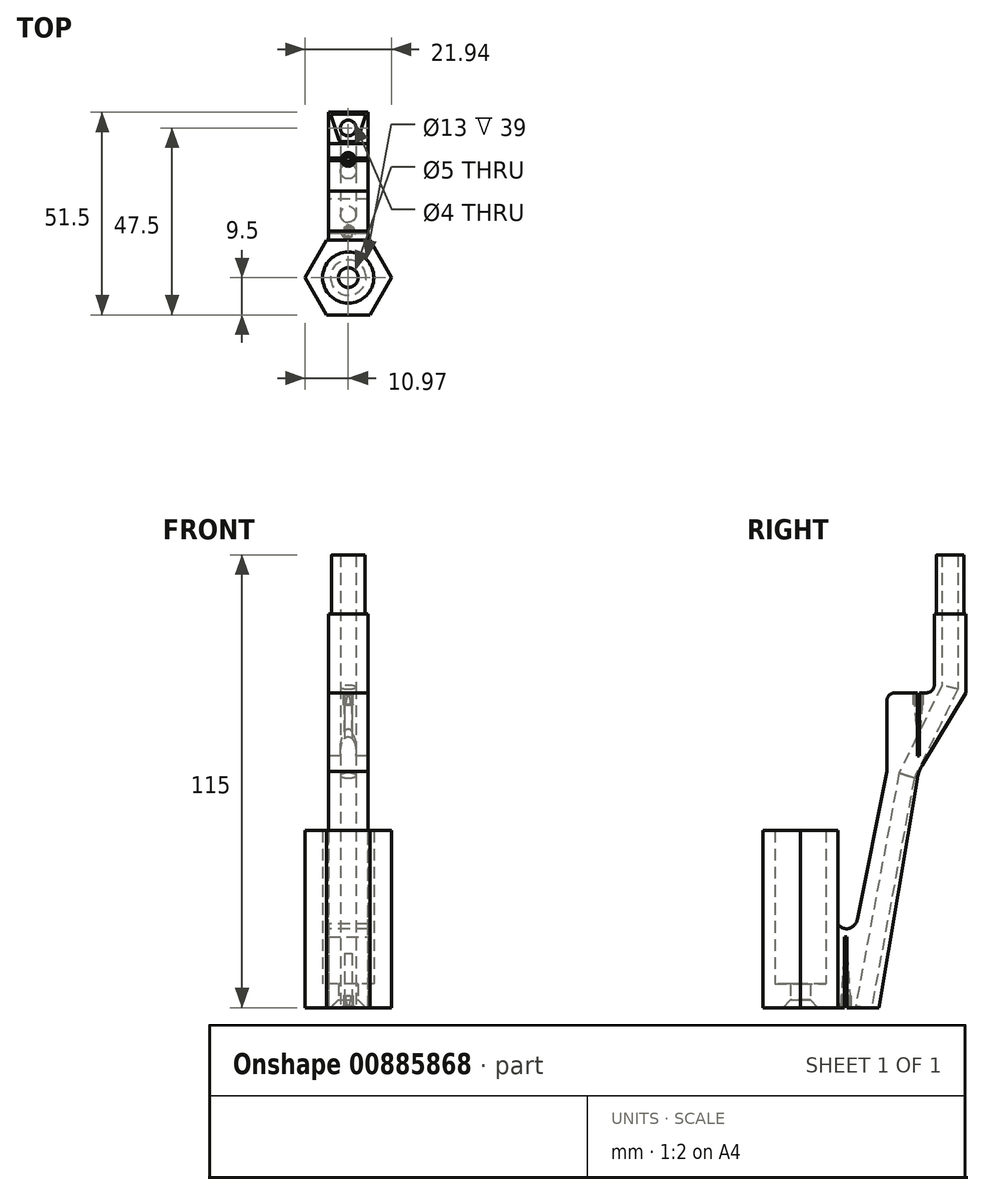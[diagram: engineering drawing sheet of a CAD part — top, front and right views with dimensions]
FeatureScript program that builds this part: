
annotation { "Feature Type Name" : "Feature", "Feature Type Description" : "" }
export const myFeature = defineFeature(function(context is Context, id is Id, definition is map)
    precondition{}
    {
        {
            var Q0;
            Q0=qCreatedBy(makeId("Top.planeOp"),FACE);
            var sketch = newSketch(context, id + "F0", { "sketchPlane" : qUnion([Q0])});
            skCircle(sketch, "E0", {"center": v(0, 0) * mm, "radius": 6.5 * mm});
            skCircle(sketch, "E1.cCircle", {"center": v(0, 0) * mm, "radius": 9.5 * mm, "construction": true});
            skLineSegment(sketch, "E1.0", {"start": v(10.97, 0) * mm, "end": v(5.48, -9.5) * mm});
            skLineSegment(sketch, "E1.1", {"start": v(5.48, -9.5) * mm, "end": v(-5.48, -9.5) * mm});
            skLineSegment(sketch, "E1.2", {"start": v(-5.48, -9.5) * mm, "end": v(-10.97, 0) * mm});
            skLineSegment(sketch, "E1.3", {"start": v(-10.97, 0) * mm, "end": v(-5.48, 9.5) * mm});
            skLineSegment(sketch, "E1.4", {"start": v(-5.48, 9.5) * mm, "end": v(5.48, 9.5) * mm});
            skLineSegment(sketch, "E1.5", {"start": v(5.48, 9.5) * mm, "end": v(10.97, 0) * mm});
            skPoint(sketch, "E1.0.midPoint", {"position": v(8.23, -4.75) * mm});
            skSolve(sketch);
        }
        {
            var Q0;
            Q0=makeQuery(id+"F0.imprint","IMPRINT",FACE,{"disambiguationData":[TD([[makeQuery(id+"F0.imprint","IMPRINT",EDGE,{"derivedFrom":sQuery(id+"F0.wireOp",EDGE,"E0")}),-1.0]])]});
            extrude(context, id + "F1", {"entities" : qUnion([Q0]), "depth" : 45 * mm, "offsetDistance" : 25 * mm});
        }
        {
            var Q0;
            Q0=makeQuery(id+"F0.imprint","IMPRINT",FACE,{"disambiguationData":[TD([[makeQuery(id+"F0.imprint","IMPRINT",EDGE,{"derivedFrom":sQuery(id+"F0.wireOp",EDGE,"E0")}),1.0]])]});
            extrude(context, id + "F2", {"entities" : qUnion([Q0]), "operationType" : NewBodyOperationType.ADD, "depth" : 6 * mm, "offsetDistance" : 25 * mm});
        }
        {
            var Q0;
            Q0=sQuery(id+"F0.wireOp",VERTEX,"E0.center");
            var Q1;
            Q1=makeQuery(id+"F1.opExtrude","SWEPT_BODY",BODY,{"disambiguationData":[OSD([sQuery(id+"F0.wireOp",EDGE,"E0"),sQuery(id+"F0.wireOp",EDGE,"E1.0"),sQuery(id+"F0.wireOp",EDGE,"E1.1"),sQuery(id+"F0.wireOp",EDGE,"E1.2"),sQuery(id+"F0.wireOp",EDGE,"E1.3"),sQuery(id+"F0.wireOp",EDGE,"E1.4"),sQuery(id+"F0.wireOp",EDGE,"E1.5")])]});
            hole(context, id + "F3", {"style" : HoleStyle.C_SINK, "endStyle" : HoleEndStyle.THROUGH, "oppositeDirection" : true, "holeDiameter" : 5 * mm, "cSinkDiameter" : 9 * mm, "cSinkAngle" : 90 * degree, "majorDiameter" : 5 * mm, "isTappedThrough" : true, "tappedDepth" : 12 * mm, "tapClearance" : 3, "locations" : qUnion([Q0]), "scope" : qUnion([Q1])});
        }
        {
            var Q0;
            Q0=qCreatedBy(makeId("Right.planeOp"),FACE);
            var sketch = newSketch(context, id + "F4", { "sketchPlane" : qUnion([Q0])});
            skLineSegment(sketch, "E2", {"start": v(0, -69.7) * mm, "end": v(0, 100) * mm, "construction": true});
            skLineSegment(sketch, "E3", {"start": v(22, 78) * mm, "end": v(22, 60) * mm});
            skLineSegment(sketch, "E4", {"start": v(34, 100) * mm, "end": v(34, 82) * mm});
            skLineSegment(sketch, "E5", {"start": v(42, 100) * mm, "end": v(34, 100) * mm});
            skLineSegment(sketch, "E6", {"start": v(22, 60) * mm, "end": v(14.48, 22.41) * mm});
            skLineSegment(sketch, "E7", {"start": v(12, 20) * mm, "end": v(11.54, 20) * mm});
            skLineSegment(sketch, "E8", {"start": v(20, 0) * mm, "end": v(29.69, 58.13) * mm});
            skLineSegment(sketch, "E9", {"start": v(32, 80) * mm, "end": v(24, 80) * mm});
            skLineSegment(sketch, "E10", {"start": v(20, 0) * mm, "end": v(8.5, 0) * mm});
            skLineSegment(sketch, "E11", {"start": v(42, 80) * mm, "end": v(30.98, 61.63) * mm});
            skLineSegment(sketch, "E12", {"start": v(42, 100) * mm, "end": v(42, 100) * mm});
            skLineSegment(sketch, "E13", {"start": v(42, 100) * mm, "end": v(42, 80) * mm});
            skPoint(sketch, "E14.visualSharp", {"position": v(20, 0) * mm});
            skPoint(sketch, "E15.visualSharp", {"position": v(30, 60) * mm});
            skArc(sketch, "E15.filletArc", {"start": v(30.98, 61.63) * mm, "mid": v(30.17, 59.94) * mm, "end": v(29.69, 58.13) * mm});
            skPoint(sketch, "E16.visualSharp", {"position": v(34, 80) * mm});
            skArc(sketch, "E16.filletArc", {"start": v(32, 80) * mm, "mid": v(33.41, 80.59) * mm, "end": v(34, 82) * mm});
            skPoint(sketch, "E17.visualSharp", {"position": v(22, 80) * mm});
            skArc(sketch, "E17.filletArc", {"start": v(24, 80) * mm, "mid": v(22.59, 79.41) * mm, "end": v(22, 78) * mm});
            skPoint(sketch, "E18.visualSharp", {"position": v(34, 100) * mm});
            skPoint(sketch, "E19.visualSharp", {"position": v(14, 20) * mm});
            skArc(sketch, "E19.filletArc", {"start": v(11.54, 20) * mm, "mid": v(13.44, 20.68) * mm, "end": v(14.48, 22.41) * mm});
            skLineSegment(sketch, "E20", {"start": v(9, 23) * mm, "end": v(9, 45) * mm});
            skPoint(sketch, "E21.visualSharp", {"position": v(9, 20) * mm});
            skArc(sketch, "E21.filletArc", {"start": v(9, 23) * mm, "mid": v(9.88, 20.88) * mm, "end": v(12, 20) * mm});
            skLineSegment(sketch, "E22", {"start": v(9, 45) * mm, "end": v(8.5, 45) * mm});
            skLineSegment(sketch, "E23", {"start": v(8.5, 45) * mm, "end": v(8.5, 0) * mm});
            skLineSegment(sketch, "E24", {"start": v(16, 0) * mm, "end": v(27, 58.98) * mm});
            skLineSegment(sketch, "E25", {"start": v(27, 58.98) * mm, "end": v(38, 81.43) * mm});
            skLineSegment(sketch, "E26", {"start": v(38, 81.43) * mm, "end": v(38, 100) * mm});
            skPoint(sketch, "E27", {"position": v(38, 100) * mm});
            skLineSegment(sketch, "E28", {"start": v(38, 100) * mm, "end": v(38, 115) * mm});
            skSolve(sketch);
        }
        {
            var Q0;
            Q0 = qSketchRegion(id + "F4", true);
            extrude(context, id + "F5", {"entities" : qUnion([Q0]), "operationType" : NewBodyOperationType.ADD, "endBound" : BoundingType.SYMMETRIC, "depth" : 10 * mm, "offsetDistance" : 25 * mm});
        }
        {
            var Q0;
            Q0=makeQuery(id+"F5.opExtrude","SWEPT_FACE",FACE,{"disambiguationData":[OSD([sQuery(id+"F4.wireOp",EDGE,"E9")])]});
            var sketch = newSketch(context, id + "F6", { "sketchPlane" : qUnion([Q0])});
            skPoint(sketch, "E29", {"position": v(0, 30) * mm});
            skLineSegment(sketch, "E30.bottom", {"start": v(5, 29.7) * mm, "end": v(-5, 29.7) * mm});
            skLineSegment(sketch, "E30.top", {"start": v(5, 30.3) * mm, "end": v(-5, 30.3) * mm});
            skLineSegment(sketch, "E30.left", {"start": v(5, 29.7) * mm, "end": v(5, 30.3) * mm});
            skLineSegment(sketch, "E30.right", {"start": v(-5, 29.7) * mm, "end": v(-5, 30.3) * mm});
            skSolve(sketch);
        }
        {
            var Q0;
            Q0=sQuery(id+"F6.wireOp",VERTEX,"E29");
            var Q1;
            Q1=makeQuery(id+"F5.opExtrude","SWEPT_BODY",BODY,{"disambiguationData":[OSD([sQuery(id+"F4.wireOp",EDGE,"E3"),sQuery(id+"F4.wireOp",EDGE,"H4g1pZ8y-bMZj-Yfp0-DUyw-PG9j3wVcMHNI"),sQuery(id+"F4.wireOp",EDGE,"ujzuVlM0-uvlb-eoDg-W0Gq-mJ8zsjEyDlQp"),sQuery(id+"F4.wireOp",EDGE,"E4"),sQuery(id+"F4.wireOp",EDGE,"iK9Z7oXa-DGHX-qq8q-kj9N-MazxaWKy61rx"),sQuery(id+"F4.wireOp",EDGE,"E5"),sQuery(id+"F4.wireOp",EDGE,"E6"),sQuery(id+"F4.wireOp",EDGE,"E7"),sQuery(id+"F4.wireOp",EDGE,"E8"),sQuery(id+"F4.wireOp",EDGE,"E9"),sQuery(id+"F4.wireOp",EDGE,"E10"),sQuery(id+"F4.wireOp",EDGE,"c5ac7997-6308-41a4-87d6-0d990d36ccd3")])]});
            var Q2;
            Q2=makeQuery(id+"F1.opExtrude","SWEPT_BODY",BODY,{"disambiguationData":[OSD([sQuery(id+"F0.wireOp",EDGE,"E0"),sQuery(id+"F0.wireOp",EDGE,"E1.0"),sQuery(id+"F0.wireOp",EDGE,"E1.1"),sQuery(id+"F0.wireOp",EDGE,"E1.2"),sQuery(id+"F0.wireOp",EDGE,"E1.3"),sQuery(id+"F0.wireOp",EDGE,"E1.4"),sQuery(id+"F0.wireOp",EDGE,"E1.5")])]});
            hole(context, id + "F7", {"style" : HoleStyle.C_SINK, "endStyle" : HoleEndStyle.BLIND, "holeDiameter" : 2.5 * mm, "cSinkDiameter" : 3.5 * mm, "cSinkAngle" : 90 * degree, "majorDiameter" : 5 * mm, "holeDepth" : 3 * mm, "isTappedThrough" : true, "tappedDepth" : 12 * mm, "tapClearance" : 3, "locations" : qUnion([Q0]), "scope" : qUnion([Q1, Q2])});
        }
        {
            var Q0;
            Q0=makeQuery(id+"F6.imprint","IMPRINT",FACE,{"disambiguationData":[TD([[makeQuery(id+"F6.imprint","IMPRINT",EDGE,{"derivedFrom":sQuery(id+"F6.wireOp",EDGE,"E30.bottom")}),-1.0]])]});
            extrude(context, id + "F8", {"entities" : qUnion([Q0]), "operationType" : NewBodyOperationType.REMOVE, "oppositeDirection" : true, "depth" : 16 * mm, "offsetDistance" : 25 * mm});
        }
        {
            var Q0;
            Q0=qCreatedBy(makeId("Right.planeOp"),FACE);
            var sketch = newSketch(context, id + "F9", { "sketchPlane" : qUnion([Q0])});
            skPoint(sketch, "E31.0", {"position": v(30, 60) * mm});
            skPoint(sketch, "E31.1", {"position": v(30, 64) * mm});
            skLineSegment(sketch, "E32", {"start": v(28.75, 79.5) * mm, "end": v(31.25, 79.5) * mm});
            skLineSegment(sketch, "E33", {"start": v(28.75, 79.5) * mm, "end": v(30, 64) * mm});
            skLineSegment(sketch, "E34", {"start": v(30, 64) * mm, "end": v(31.25, 79.5) * mm});
            skPoint(sketch, "E35.0", {"position": v(28.75, 79.5) * mm});
            skPoint(sketch, "E35.1", {"position": v(31.25, 79.5) * mm});
            skSolve(sketch);
        }
        {
            var Q0;
            Q0 = qSketchRegion(id + "F9", true);
            extrude(context, id + "F10", {"entities" : qUnion([Q0]), "operationType" : NewBodyOperationType.REMOVE, "endBound" : BoundingType.SYMMETRIC, "depth" : 2 * mm, "offsetDistance" : 25 * mm});
        }
        {
            var Q0;
            Q0=makeQuery(id+"F5.opExtrude","SWEPT_FACE",FACE,{"disambiguationData":[OSD([sQuery(id+"F4.wireOp",EDGE,"E10")])]});
            var sketch = newSketch(context, id + "F11", { "sketchPlane" : qUnion([Q0])});
            skLineSegment(sketch, "E36", {"start": v(-5, -11.24) * mm, "end": v(5, -11.24) * mm});
            skLineSegment(sketch, "E37", {"start": v(5, -11.24) * mm, "end": v(5, -11.84) * mm});
            skLineSegment(sketch, "E38", {"start": v(5, -11.84) * mm, "end": v(-5, -11.84) * mm});
            skLineSegment(sketch, "E39", {"start": v(-5, -11.84) * mm, "end": v(-5, -11.24) * mm});
            skLineSegment(sketch, "E40", {"start": v(0, -11.24) * mm, "end": v(0, -11.84) * mm, "construction": true});
            skPoint(sketch, "E41", {"position": v(0, -11.54) * mm});
            skSolve(sketch);
        }
        {
            var Q0;
            Q0=sQuery(id+"F11.wireOp",VERTEX,"E41");
            var Q1;
            Q1=makeQuery(id+"F5.opExtrude","SWEPT_BODY",BODY,{"disambiguationData":[OSD([sQuery(id+"F4.wireOp",EDGE,"E3"),sQuery(id+"F4.wireOp",EDGE,"H4g1pZ8y-bMZj-Yfp0-DUyw-PG9j3wVcMHNI"),sQuery(id+"F4.wireOp",EDGE,"ujzuVlM0-uvlb-eoDg-W0Gq-mJ8zsjEyDlQp"),sQuery(id+"F4.wireOp",EDGE,"E4"),sQuery(id+"F4.wireOp",EDGE,"iK9Z7oXa-DGHX-qq8q-kj9N-MazxaWKy61rx"),sQuery(id+"F4.wireOp",EDGE,"E5"),sQuery(id+"F4.wireOp",EDGE,"E6"),sQuery(id+"F4.wireOp",EDGE,"E7"),sQuery(id+"F4.wireOp",EDGE,"E8"),sQuery(id+"F4.wireOp",EDGE,"E9"),sQuery(id+"F4.wireOp",EDGE,"E10"),sQuery(id+"F4.wireOp",EDGE,"c5ac7997-6308-41a4-87d6-0d990d36ccd3")])]});
            var Q2;
            Q2=makeQuery(id+"F1.opExtrude","SWEPT_BODY",BODY,{"disambiguationData":[OSD([sQuery(id+"F0.wireOp",EDGE,"E0"),sQuery(id+"F0.wireOp",EDGE,"E1.0"),sQuery(id+"F0.wireOp",EDGE,"E1.1"),sQuery(id+"F0.wireOp",EDGE,"E1.2"),sQuery(id+"F0.wireOp",EDGE,"E1.3"),sQuery(id+"F0.wireOp",EDGE,"E1.4"),sQuery(id+"F0.wireOp",EDGE,"E1.5")])]});
            hole(context, id + "F12", {"style" : HoleStyle.C_SINK, "endStyle" : HoleEndStyle.BLIND, "holeDiameter" : 2.5 * mm, "cSinkDiameter" : 3.5 * mm, "cSinkAngle" : 90 * degree, "majorDiameter" : 5 * mm, "holeDepth" : 3 * mm, "isTappedThrough" : true, "tappedDepth" : 12 * mm, "tapClearance" : 3, "locations" : qUnion([Q0]), "scope" : qUnion([Q1, Q2])});
        }
        {
            var Q0;
            Q0=makeQuery(id+"F11.imprint","IMPRINT",FACE,{"disambiguationData":[TD([[makeQuery(id+"F11.imprint","IMPRINT",EDGE,{"derivedFrom":sQuery(id+"F11.wireOp",EDGE,"E36")}),-1.0]])]});
            extrude(context, id + "F13", {"entities" : qUnion([Q0]), "operationType" : NewBodyOperationType.REMOVE, "oppositeDirection" : true, "depth" : 18 * mm, "offsetDistance" : 25 * mm});
        }
        {
            var Q0;
            Q0=qCreatedBy(makeId("Right.planeOp"),FACE);
            var sketch = newSketch(context, id + "F14", { "sketchPlane" : qUnion([Q0])});
            skPoint(sketch, "E42.0", {"position": v(10.3, 0.5) * mm});
            skPoint(sketch, "E42.1", {"position": v(12.8, 0.5) * mm});
            skPoint(sketch, "E43.0", {"position": v(11.84, 18) * mm});
            skPoint(sketch, "E44.0", {"position": v(11.24, 18) * mm});
            skLineSegment(sketch, "E45", {"start": v(11.24, 18) * mm, "end": v(11.84, 18) * mm, "construction": true});
            skPoint(sketch, "E46", {"position": v(11.54, 18) * mm});
            skLineSegment(sketch, "E47", {"start": v(10.3, 0.5) * mm, "end": v(11.54, 18) * mm});
            skLineSegment(sketch, "E48", {"start": v(11.54, 18) * mm, "end": v(12.8, 0.5) * mm});
            skLineSegment(sketch, "E49", {"start": v(10.3, 0.5) * mm, "end": v(12.8, 0.5) * mm});
            skSolve(sketch);
        }
        {
            var Q0;
            Q0 = qSketchRegion(id + "F14", true);
            extrude(context, id + "F15", {"entities" : qUnion([Q0]), "operationType" : NewBodyOperationType.REMOVE, "endBound" : BoundingType.SYMMETRIC, "depth" : 2 * mm, "offsetDistance" : 25 * mm});
        }
        {
            var Q0;
            Q0=makeQuery(id+"F5.opExtrude","SWEPT_FACE",FACE,{"disambiguationData":[OSD([sQuery(id+"F4.wireOp",EDGE,"E5")])]});
            var sketch = newSketch(context, id + "F16", { "sketchPlane" : qUnion([Q0])});
            skLineSegment(sketch, "E50", {"start": v(-3.68, 41.5) * mm, "end": v(3.68, 41.5) * mm});
            skLineSegment(sketch, "E51", {"start": v(4.25, 40.72) * mm, "end": v(2.38, 34.92) * mm});
            skLineSegment(sketch, "E52", {"start": v(1.81, 34.5) * mm, "end": v(-1.81, 34.5) * mm});
            skLineSegment(sketch, "E53", {"start": v(-2.38, 34.92) * mm, "end": v(-4.25, 40.72) * mm});
            skPoint(sketch, "E54.visualSharp", {"position": v(-4.5, 41.5) * mm});
            skArc(sketch, "E54.filletArc", {"start": v(-3.68, 41.5) * mm, "mid": v(-4.16, 41.25) * mm, "end": v(-4.25, 40.72) * mm});
            skPoint(sketch, "E55.visualSharp", {"position": v(4.5, 41.5) * mm});
            skArc(sketch, "E55.filletArc", {"start": v(4.25, 40.72) * mm, "mid": v(4.16, 41.25) * mm, "end": v(3.68, 41.5) * mm});
            skPoint(sketch, "E56.visualSharp", {"position": v(2.25, 34.5) * mm});
            skArc(sketch, "E56.filletArc", {"start": v(1.81, 34.5) * mm, "mid": v(2.17, 34.62) * mm, "end": v(2.38, 34.92) * mm});
            skPoint(sketch, "E57.visualSharp", {"position": v(-2.25, 34.5) * mm});
            skArc(sketch, "E57.filletArc", {"start": v(-2.38, 34.92) * mm, "mid": v(-2.17, 34.62) * mm, "end": v(-1.81, 34.5) * mm});
            skPoint(sketch, "E58", {"position": v(0, 42) * mm});
            skPoint(sketch, "E59", {"position": v(0, 34) * mm});
            skLineSegment(sketch, "E60", {"start": v(0, 42) * mm, "end": v(0, 34) * mm, "construction": true});
            skPoint(sketch, "E61", {"position": v(0, 41.5) * mm});
            skPoint(sketch, "E62", {"position": v(0, 34.5) * mm});
            skSolve(sketch);
        }
        {
            var Q0;
            Q0=makeQuery(id+"F16.imprint","IMPRINT",FACE,{"disambiguationData":[TD([[makeQuery(id+"F16.imprint","IMPRINT",EDGE,{"derivedFrom":sQuery(id+"F16.wireOp",EDGE,"E50")}),-1.0]])]});
            extrude(context, id + "F17", {"entities" : qUnion([Q0]), "operationType" : NewBodyOperationType.ADD, "depth" : 15 * mm, "offsetDistance" : 25 * mm});
        }
        {
            var Q0;
            {var subQ10=sQuery(id+"F4.wireOp",EDGE,"E10");var subQ12=sQuery(id+"F4.wireOp",EDGE,"E8");Q0=makeQuery(id+"F13.boolean.opBoolean","SPLIT",FACE,{"disambiguationData":[TD([makeQuery(id+"F5.opExtrude","SWEPT_FACE",FACE,{"disambiguationData":[OSD([subQ12])]})])],"derivedFrom":makeQuery(id+"F5.opExtrude","SWEPT_FACE",FACE,{"disambiguationData":[OSD([subQ10])]})});}
            var sketch = newSketch(context, id + "F18", { "sketchPlane" : qUnion([Q0])});
            skPoint(sketch, "E63", {"position": v(0, -16) * mm});
            skCircle(sketch, "E64", {"center": v(0, -16) * mm, "radius": 2 * mm});
            skSolve(sketch);
        }
        {
            var Q0;
            Q0=makeQuery(id+"F17.opExtrude","CAP_FACE",FACE,{"disambiguationData":[OSD([sQuery(id+"F16.wireOp",EDGE,"E50"),sQuery(id+"F16.wireOp",EDGE,"E51"),sQuery(id+"F16.wireOp",EDGE,"E52"),sQuery(id+"F16.wireOp",EDGE,"E53"),sQuery(id+"F16.wireOp",EDGE,"E54.filletArc"),sQuery(id+"F16.wireOp",EDGE,"E55.filletArc"),sQuery(id+"F16.wireOp",EDGE,"E56.filletArc"),sQuery(id+"F16.wireOp",EDGE,"E57.filletArc")])],"isStart":false});
            var sketch = newSketch(context, id + "F19", { "sketchPlane" : qUnion([Q0])});
            skCircle(sketch, "E65", {"center": v(0, 38) * mm, "radius": 2 * mm});
            skSolve(sketch);
        }
        {
            var Q0;
            Q0=makeQuery(id+"F18.imprint","IMPRINT",FACE,{"disambiguationData":[TD([[makeQuery(id+"F18.imprint","IMPRINT",EDGE,{"derivedFrom":sQuery(id+"F18.wireOp",EDGE,"E64")}),1.0]])]});
            var Q1;
            Q1=makeQuery(id+"F19.imprint","IMPRINT",FACE,{"disambiguationData":[TD([[makeQuery(id+"F19.imprint","IMPRINT",EDGE,{"derivedFrom":sQuery(id+"F19.wireOp",EDGE,"E65")}),1.0]])]});
            var Q2;
            Q2=sQuery(id+"F18.wireOp",EDGE,"cbpow5Sv-7AYt-Mp7k-YbMw-OIgniC9jwkgQ");
            var Q3;
            Q3=sQuery(id+"F19.wireOp",EDGE,"E65");
            var Q4;
            Q4=sQuery(id+"F4.wireOp",EDGE,"E24");
            var Q5;
            Q5=sQuery(id+"F4.wireOp",EDGE,"E25");
            var Q6;
            Q6=sQuery(id+"F4.wireOp",EDGE,"E26");
            var Q7;
            Q7=sQuery(id+"F4.wireOp",EDGE,"E28");
            sweep(context, id + "F20", {"operationType" : NewBodyOperationType.REMOVE, "profiles" : qUnion([Q0, Q1]), "surfaceProfiles" : qUnion([Q2, Q3]), "path" : qUnion([Q4, Q5, Q6, Q7])});
        }
    });
